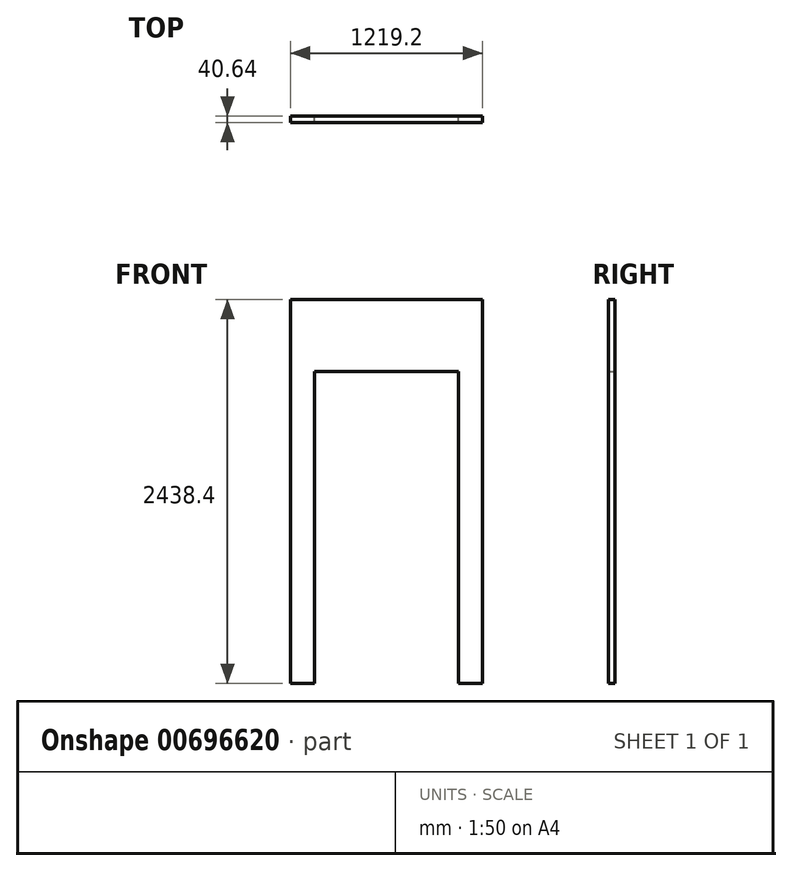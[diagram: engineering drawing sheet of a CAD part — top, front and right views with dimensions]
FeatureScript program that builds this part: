
annotation { "Feature Type Name" : "Feature", "Feature Type Description" : "" }
export const myFeature = defineFeature(function(context is Context, id is Id, definition is map)
    precondition{}
    {
        {
            var Q0;
            Q0=qCreatedBy(makeId("Front.planeOp"),FACE);
            var sketch = newSketch(context, id + "F0", { "sketchPlane" : qUnion([Q0])});
            skLineSegment(sketch, "E0.bottom", {"start": v(0, 0) * mm, "end": v(-1219.2, 0) * mm});
            skLineSegment(sketch, "E0.top", {"start": v(0, 2438.4) * mm, "end": v(-1219.2, 2438.4) * mm});
            skLineSegment(sketch, "E0.left", {"start": v(0, 0) * mm, "end": v(0, 2438.4) * mm});
            skLineSegment(sketch, "E0.right", {"start": v(-1219.2, 0) * mm, "end": v(-1219.2, 2438.4) * mm});
            skLineSegment(sketch, "E1.bottom", {"start": v(-152.4, 0) * mm, "end": v(-1066.8, 0) * mm});
            skLineSegment(sketch, "E1.top", {"start": v(-152.4, 1981.2) * mm, "end": v(-1066.8, 1981.2) * mm});
            skLineSegment(sketch, "E1.left", {"start": v(-152.4, 0) * mm, "end": v(-152.4, 1981.2) * mm});
            skLineSegment(sketch, "E1.right", {"start": v(-1066.8, 0) * mm, "end": v(-1066.8, 1981.2) * mm});
            skSolve(sketch);
        }
        {
            var Q0;
            Q0=makeQuery(id+"F0.imprint","IMPRINT",FACE,{"disambiguationData":[TD([[makeQuery(id+"F0.imprint","IMPRINT",EDGE,{"derivedFrom":sQuery(id+"F0.wireOp",EDGE,"E0.top")}),1.0]])]});
            extrude(context, id + "F1", {"entities" : qUnion([Q0]), "depth" : 40.64 * mm, "offsetDistance" : 25.4 * mm});
        }
    });
